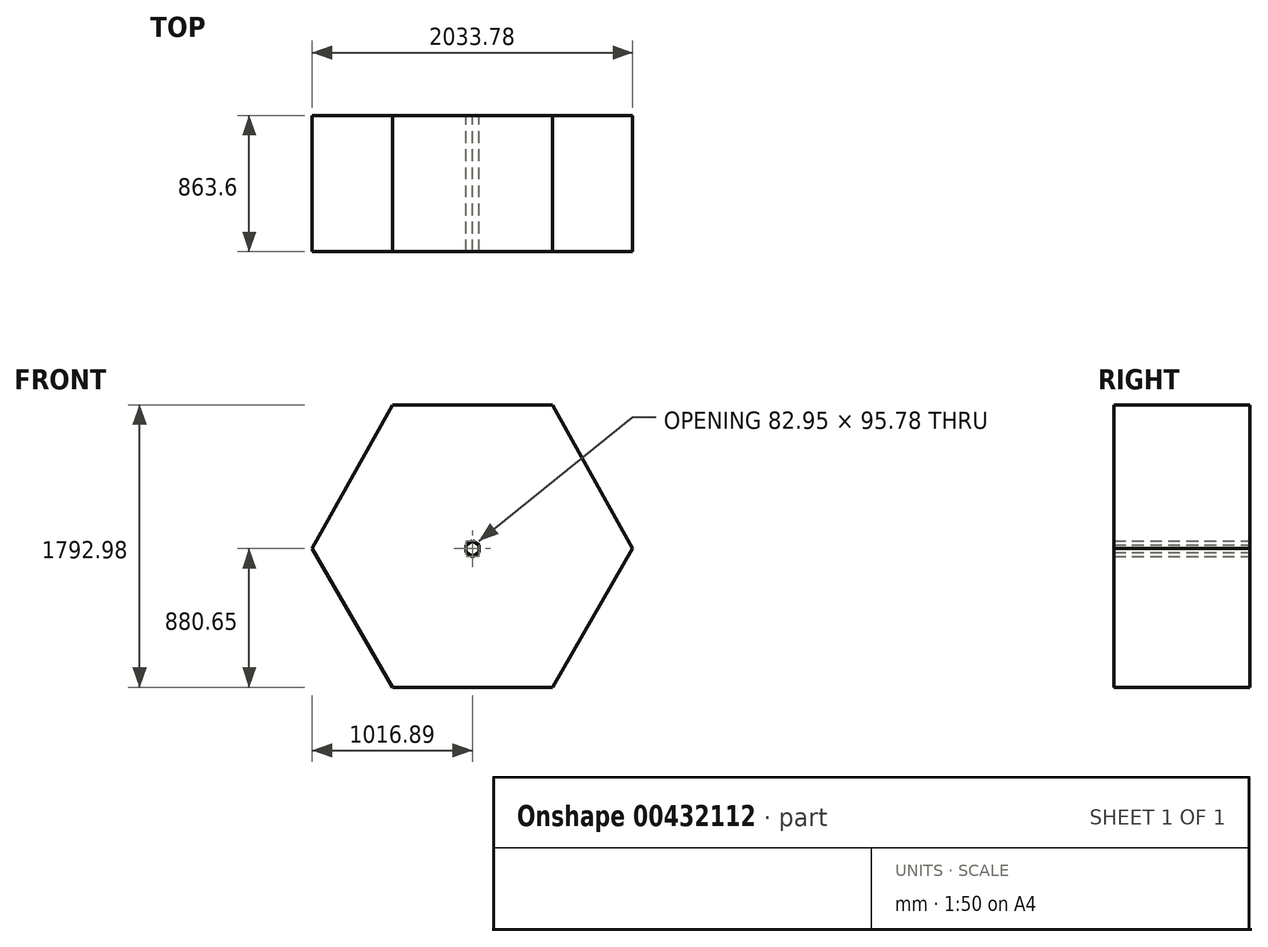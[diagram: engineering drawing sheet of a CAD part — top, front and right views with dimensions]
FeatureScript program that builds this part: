
annotation { "Feature Type Name" : "Feature", "Feature Type Description" : "" }
export const myFeature = defineFeature(function(context is Context, id is Id, definition is map)
    precondition{}
    {
        {
            var Q0;
            Q0=qCreatedBy(makeId("Front.planeOp"),FACE);
            var sketch = newSketch(context, id + "F0", { "sketchPlane" : qUnion([Q0])});
            skLineSegment(sketch, "E0.0", {"start": v(1016.89, 0) * mm, "end": v(508.44, -880.65) * mm});
            skLineSegment(sketch, "E0.1", {"start": v(508.44, -880.65) * mm, "end": v(-508.44, -880.65) * mm});
            skLineSegment(sketch, "E0.2", {"start": v(-508.44, -880.65) * mm, "end": v(-1016.89, 0) * mm});
            skLineSegment(sketch, "E0.3", {"start": v(-1016.89, 0) * mm, "end": v(-508.44, 912.33) * mm});
            skLineSegment(sketch, "E0.4", {"start": v(-508.44, 912.33) * mm, "end": v(508.44, 912.33) * mm});
            skLineSegment(sketch, "E0.5", {"start": v(508.44, 912.33) * mm, "end": v(1016.89, 0) * mm});
            skCircle(sketch, "E1.cCircle", {"center": v(0, 0) * mm, "radius": 41.48 * mm, "construction": true});
            skLineSegment(sketch, "E1.0", {"start": v(41.48, 23.95) * mm, "end": v(41.48, -23.95) * mm});
            skLineSegment(sketch, "E1.1", {"start": v(41.48, -23.95) * mm, "end": v(0, -47.9) * mm});
            skLineSegment(sketch, "E1.2", {"start": v(0, -47.9) * mm, "end": v(-41.48, -23.95) * mm});
            skLineSegment(sketch, "E1.3", {"start": v(-41.48, -23.95) * mm, "end": v(-41.48, 23.95) * mm});
            skLineSegment(sketch, "E1.4", {"start": v(-41.48, 23.95) * mm, "end": v(0, 47.9) * mm});
            skLineSegment(sketch, "E1.5", {"start": v(0, 47.9) * mm, "end": v(41.48, 23.95) * mm});
            skPoint(sketch, "E1.0.midPoint", {"position": v(41.48, 0) * mm});
            skSolve(sketch);
        }
        {
            var Q0;
            Q0 = qSketchRegion(id + "F0", true);
            extrude(context, id + "F1", {"entities" : qUnion([Q0]), "depth" : 863.6 * mm});
        }
    });
